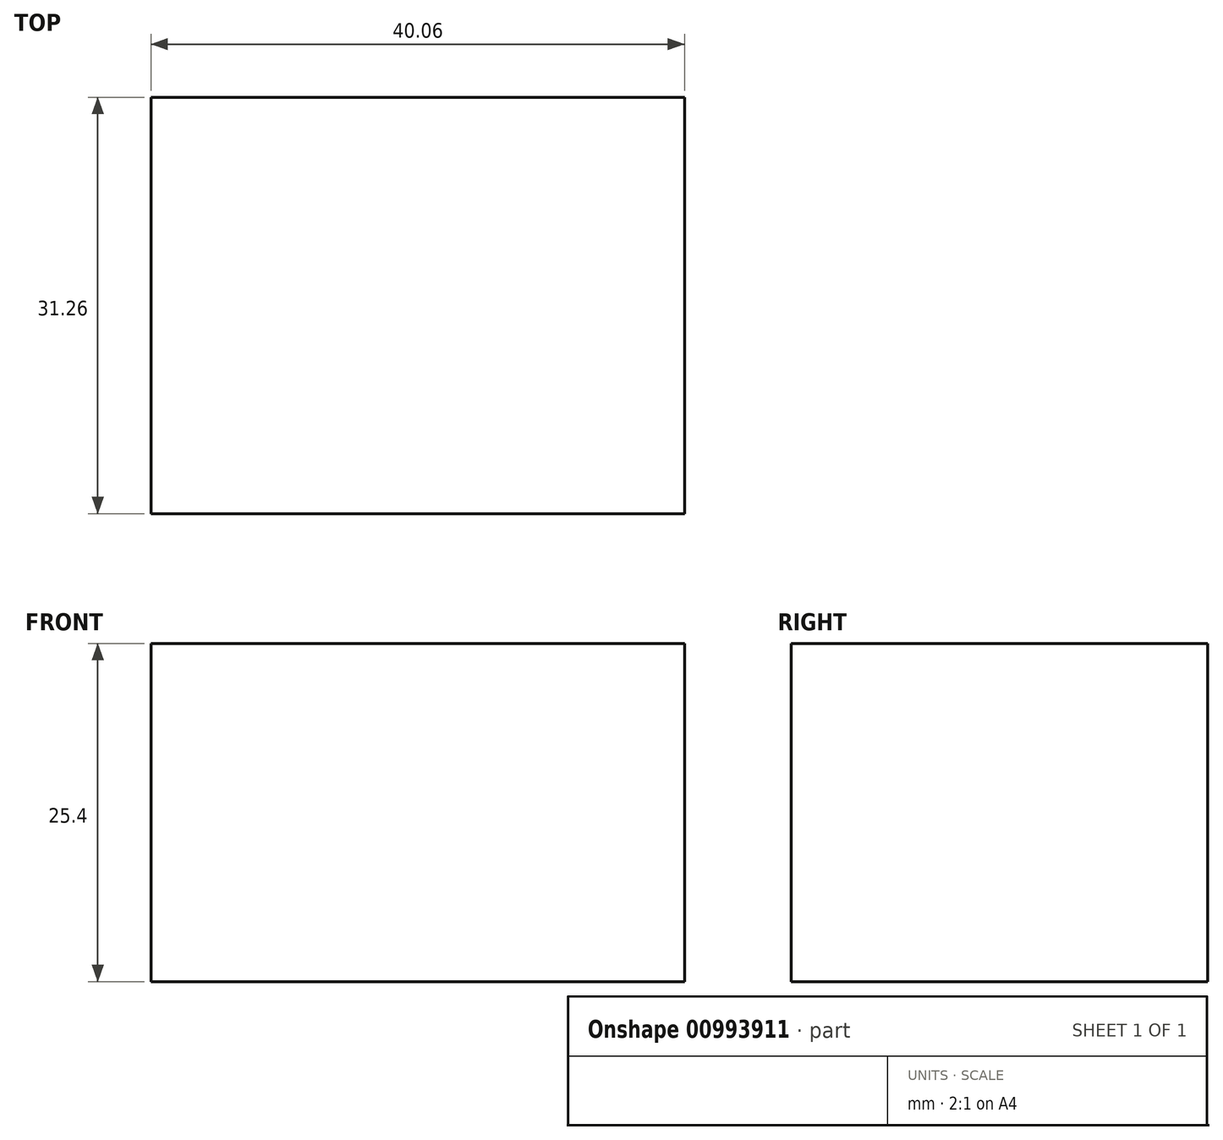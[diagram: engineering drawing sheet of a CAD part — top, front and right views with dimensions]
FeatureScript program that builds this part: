
annotation { "Feature Type Name" : "Feature", "Feature Type Description" : "" }
export const myFeature = defineFeature(function(context is Context, id is Id, definition is map)
    precondition{}
    {
        {
            var Q0;
            Q0=qCreatedBy(makeId("Top.planeOp"),FACE);
            var sketch = newSketch(context, id + "F0", { "sketchPlane" : qUnion([Q0])});
            skLineSegment(sketch, "E0.bottom", {"start": v(20.03, -15.63) * mm, "end": v(-20.03, -15.63) * mm});
            skLineSegment(sketch, "E0.top", {"start": v(20.03, 15.63) * mm, "end": v(-20.03, 15.63) * mm});
            skLineSegment(sketch, "E0.left", {"start": v(20.03, -15.63) * mm, "end": v(20.03, 15.63) * mm});
            skLineSegment(sketch, "E0.right", {"start": v(-20.03, -15.63) * mm, "end": v(-20.03, 15.63) * mm});
            skPoint(sketch, "E0.middle", {"position": v(0, 0) * mm});
            skSolve(sketch);
        }
        {
            var Q0;
            Q0=makeQuery(id+"F0.imprint","IMPRINT",FACE,{"disambiguationData":[TD([[makeQuery(id+"F0.imprint","IMPRINT",EDGE,{"derivedFrom":sQuery(id+"F0.wireOp",EDGE,"E0.bottom")}),-1.0]])]});
            extrude(context, id + "F1", {"entities" : qUnion([Q0]), "depth" : 25.4 * mm, "offsetDistance" : 25.4 * mm});
        }
    });
